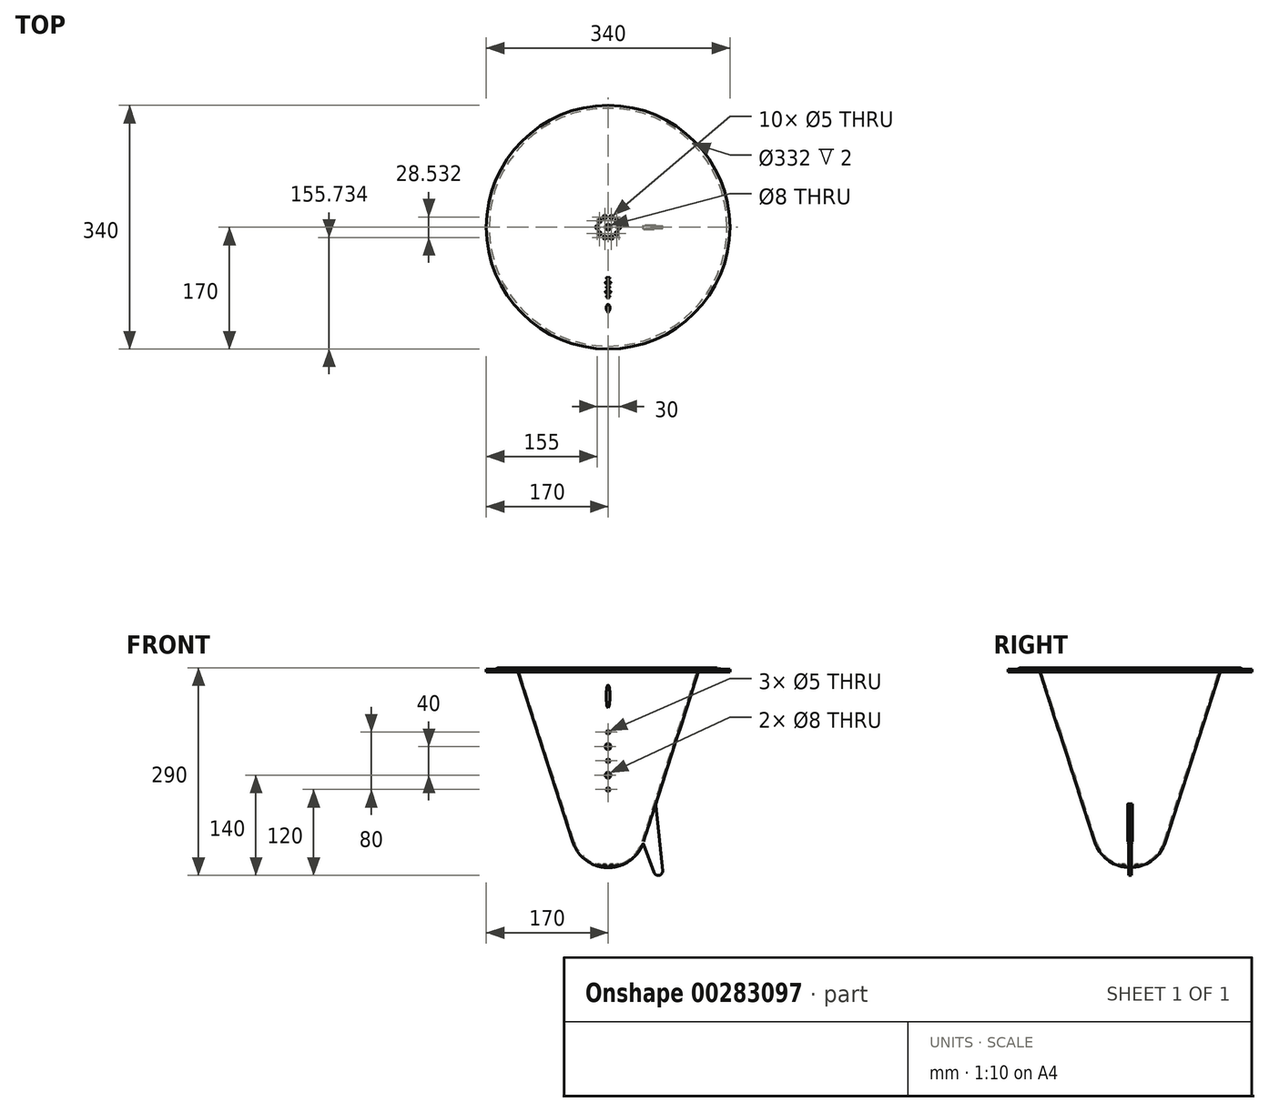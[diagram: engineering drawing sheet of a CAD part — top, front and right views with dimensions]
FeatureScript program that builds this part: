
annotation { "Feature Type Name" : "Feature", "Feature Type Description" : "" }
export const myFeature = defineFeature(function(context is Context, id is Id, definition is map)
    precondition{}
    {
        {
            var Q0;
            Q0=qCreatedBy(makeId("Front.planeOp"),FACE);
            var sketch = newSketch(context, id + "F0", { "sketchPlane" : qUnion([Q0])});
            skArc(sketch, "E0", {"start": v(0, -275) * mm, "mid": v(29.44, -265.41) * mm, "end": v(47.6, -240.33) * mm});
            skLineSegment(sketch, "E1", {"start": v(128.28, 0) * mm, "end": v(133.37, 0) * mm});
            skLineSegment(sketch, "E2.0", {"start": v(24.32, 2) * mm, "end": v(176.57, 2) * mm, "construction": true});
            skArc(sketch, "E3", {"start": v(155.32, 1) * mm, "mid": v(151.83, 2) * mm, "end": v(148.4, 0.8) * mm});
            skArc(sketch, "E4", {"start": v(143.6, 0.8) * mm, "mid": v(140.17, 2) * mm, "end": v(136.68, 1) * mm});
            skArc(sketch, "E5.trimOffspring", {"start": v(143.6, 0.8) * mm, "mid": v(146, 0) * mm, "end": v(148.4, 0.8) * mm});
            skLineSegment(sketch, "E6.trimOffspring", {"start": v(158.63, 0) * mm, "end": v(170, 0) * mm});
            skLineSegment(sketch, "E7", {"start": v(170, 0) * mm, "end": v(170, -4) * mm});
            skLineSegment(sketch, "E8", {"start": v(170, -4) * mm, "end": v(166, -4) * mm});
            skLineSegment(sketch, "E9", {"start": v(166, -4) * mm, "end": v(166, -2) * mm});
            skPoint(sketch, "E10.visualSharp", {"position": v(135.53, 0) * mm});
            skArc(sketch, "E10.filletArc", {"start": v(133.37, 0) * mm, "mid": v(135.1, 0.26) * mm, "end": v(136.68, 1) * mm});
            skPoint(sketch, "E11.visualSharp", {"position": v(156.47, 0) * mm});
            skArc(sketch, "E11.filletArc", {"start": v(155.32, 1) * mm, "mid": v(156.9, 0.26) * mm, "end": v(158.63, 0) * mm});
            skArc(sketch, "E12.0", {"start": v(154.21, -0.67) * mm, "mid": v(156.32, -1.66) * mm, "end": v(158.63, -2) * mm});
            skArc(sketch, "E12.1", {"start": v(154.21, -0.67) * mm, "mid": v(151.88, 0) * mm, "end": v(149.6, -0.8) * mm});
            skLineSegment(sketch, "E12.2", {"start": v(128.28, -2) * mm, "end": v(133.37, -2) * mm});
            skArc(sketch, "E12.3", {"start": v(133.37, -2) * mm, "mid": v(135.68, -1.66) * mm, "end": v(137.79, -0.67) * mm});
            skArc(sketch, "E12.4", {"start": v(142.4, -0.8) * mm, "mid": v(140.12, 0) * mm, "end": v(137.79, -0.67) * mm});
            skArc(sketch, "E12.5", {"start": v(142.4, -0.8) * mm, "mid": v(146, -2) * mm, "end": v(149.6, -0.8) * mm});
            skLineSegment(sketch, "E13", {"start": v(166, -2) * mm, "end": v(158.63, -2) * mm});
            skLineSegment(sketch, "E14", {"start": v(124, -3.12) * mm, "end": v(47.6, -240.33) * mm});
            skLineSegment(sketch, "E15", {"start": v(0, -225) * mm, "end": v(0, -275) * mm, "construction": true});
            skLineSegment(sketch, "E16.0", {"start": v(125.9, -3.73) * mm, "end": v(49.5, -240.94) * mm});
            skArc(sketch, "E16.1", {"start": v(0, -277) * mm, "mid": v(30.62, -267.03) * mm, "end": v(49.5, -240.94) * mm});
            skLineSegment(sketch, "E17", {"start": v(0, -275) * mm, "end": v(0, -277) * mm});
            skArc(sketch, "E18.filletArc", {"start": v(128.28, -2) * mm, "mid": v(126.8, -2.48) * mm, "end": v(125.9, -3.73) * mm});
            skPoint(sketch, "E19.visualSharp", {"position": v(125, 0) * mm});
            skArc(sketch, "E19.filletArc", {"start": v(128.28, 0) * mm, "mid": v(125.63, -0.86) * mm, "end": v(124, -3.12) * mm});
            skSolve(sketch);
        }
        {
            var Q0;
            Q0 = qSketchRegion(id + "F0", true);
            var Q1;
            Q1=sQuery(id+"F0.wireOp",EDGE,"E15");
            revolve(context, id + "F1", {"entities" : qUnion([Q0]), "axis" : qUnion([Q1]), "revolveType" : RevolveType.FULL});
        }
        {
            var Q0;
            Q0=qCreatedBy(makeId("Top.planeOp"),FACE);
            var sketch = newSketch(context, id + "F2", { "sketchPlane" : qUnion([Q0])});
            skCircle(sketch, "E20", {"center": v(0, 0) * mm, "radius": 4 * mm});
            skCircle(sketch, "E21", {"center": v(15, 0) * mm, "radius": 2.5 * mm});
            skCircle(sketch, "E22.1.0", {"center": v(12.14, 8.82) * mm, "radius": 2.5 * mm});
            skCircle(sketch, "E22.2.0", {"center": v(4.64, 14.27) * mm, "radius": 2.5 * mm});
            skCircle(sketch, "E22.3.0", {"center": v(-4.64, 14.27) * mm, "radius": 2.5 * mm});
            skCircle(sketch, "E22.4.0", {"center": v(-12.14, 8.82) * mm, "radius": 2.5 * mm});
            skCircle(sketch, "E22.5.0", {"center": v(-15, 0) * mm, "radius": 2.5 * mm});
            skCircle(sketch, "E22.6.0", {"center": v(-12.14, -8.82) * mm, "radius": 2.5 * mm});
            skCircle(sketch, "E22.7.0", {"center": v(-4.64, -14.27) * mm, "radius": 2.5 * mm});
            skCircle(sketch, "E22.8.0", {"center": v(4.64, -14.27) * mm, "radius": 2.5 * mm});
            skCircle(sketch, "E22.9.0", {"center": v(12.14, -8.82) * mm, "radius": 2.5 * mm});
            skSolve(sketch);
        }
        {
            var Q0;
            Q0 = qSketchRegion(id + "F2", true);
            extrude(context, id + "F3", {"entities" : qUnion([Q0]), "operationType" : NewBodyOperationType.REMOVE, "endBound" : BoundingType.THROUGH_ALL, "oppositeDirection" : true, "depth" : 25 * mm});
        }
        {
            var Q0;
            Q0=qCreatedBy(makeId("Front.planeOp"),FACE);
            var sketch = newSketch(context, id + "F4", { "sketchPlane" : qUnion([Q0])});
            skLineSegment(sketch, "E23", {"start": v(0, 0) * mm, "end": v(0, -185.64) * mm, "construction": true});
            skEllipse(sketch, "E24", {"center": v(0, -38) * mm, "majorRadius": 16 * mm, "minorRadius": 2.5 * mm, "majorAxis": v(0, -1)});
            skCircle(sketch, "E25", {"center": v(0, -168) * mm, "radius": 2.5 * mm});
            skCircle(sketch, "E26", {"center": v(0, -88) * mm, "radius": 2.5 * mm});
            skCircle(sketch, "E27", {"center": v(0, -148) * mm, "radius": 4 * mm});
            skCircle(sketch, "E28", {"center": v(0, -128) * mm, "radius": 2.5 * mm});
            skCircle(sketch, "E29", {"center": v(0, -108) * mm, "radius": 4 * mm});
            skSolve(sketch);
        }
        {
            var Q0;
            Q0 = qSketchRegion(id + "F4", true);
            extrude(context, id + "F5", {"entities" : qUnion([Q0]), "operationType" : NewBodyOperationType.REMOVE, "endBound" : BoundingType.THROUGH_ALL, "depth" : 25 * mm});
        }
        {
            var Q0;
            Q0=qCreatedBy(makeId("Front.planeOp"),FACE);
            var sketch = newSketch(context, id + "F6", { "sketchPlane" : qUnion([Q0])});
            skLineSegment(sketch, "E30.0", {"start": v(66.55, -188) * mm, "end": v(49.5, -240.94) * mm});
            skArc(sketch, "E31.0", {"start": v(0, -277) * mm, "mid": v(30.62, -267.03) * mm, "end": v(49.5, -240.94) * mm});
            skLineSegment(sketch, "E32", {"start": v(66.55, -188) * mm, "end": v(75.97, -281.4) * mm});
            skArc(sketch, "E33", {"start": v(64.4, -284.13) * mm, "mid": v(71.38, -287.84) * mm, "end": v(75.97, -281.4) * mm});
            skLineSegment(sketch, "E34", {"start": v(70, -288) * mm, "end": v(129.27, -288) * mm, "construction": true});
            skLineSegment(sketch, "E35", {"start": v(48.79, -243) * mm, "end": v(64.4, -284.13) * mm});
            skLineSegment(sketch, "E36.0", {"start": v(24.32, 2) * mm, "end": v(176.57, 2) * mm, "construction": true});
            skLineSegment(sketch, "E37.0", {"start": v(66.55, -184.74) * mm, "end": v(48.54, -240.64) * mm});
            skLineSegment(sketch, "E38", {"start": v(48.79, -243) * mm, "end": v(48.54, -240.64) * mm});
            skLineSegment(sketch, "E39", {"start": v(66.55, -188) * mm, "end": v(66.55, -184.74) * mm});
            skPoint(sketch, "E40.orphan", {"position": v(125.9, -3.73) * mm});
            skSolve(sketch);
        }
        {
            var Q0;
            Q0 = qSketchRegion(id + "F6", true);
            extrude(context, id + "F7", {"entities" : qUnion([Q0]), "operationType" : NewBodyOperationType.ADD, "endBound" : BoundingType.SYMMETRIC, "depth" : 4 * mm});
        }
        {
            var Q0;
            Q0=makeQuery(id+"FGJo6OA5AEpU7Sm_1.2.F7.boolean.opBoolean","INTERSECT",EDGE,{"derivedFrom":[makeQuery(id+"F1.opRevolve","SWEPT_FACE",FACE,{"disambiguationData":[OSD([sQuery(id+"F0.wireOp",EDGE,"E16.0")])]}),makeQuery(id+"FGJo6OA5AEpU7Sm_1.2.F7.opExtrude","CAP_FACE",FACE,{"disambiguationData":[OSD([sQuery(id+"F6.wireOp",EDGE,"E32"),sQuery(id+"F6.wireOp",EDGE,"E33"),sQuery(id+"F6.wireOp",EDGE,"E35"),sQuery(id+"F6.wireOp",EDGE,"E37.0"),sQuery(id+"F6.wireOp",EDGE,"E38"),sQuery(id+"F6.wireOp",EDGE,"E39")])],"isStart":true})]});
            var Q1;
            Q1=makeQuery(id+"FGJo6OA5AEpU7Sm_1.1.F7.boolean.opBoolean","INTERSECT",EDGE,{"derivedFrom":[makeQuery(id+"F1.opRevolve","SWEPT_FACE",FACE,{"disambiguationData":[OSD([sQuery(id+"F0.wireOp",EDGE,"E16.0")])]}),makeQuery(id+"FGJo6OA5AEpU7Sm_1.1.F7.opExtrude","CAP_FACE",FACE,{"disambiguationData":[OSD([sQuery(id+"F6.wireOp",EDGE,"E32"),sQuery(id+"F6.wireOp",EDGE,"E33"),sQuery(id+"F6.wireOp",EDGE,"E35"),sQuery(id+"F6.wireOp",EDGE,"E37.0"),sQuery(id+"F6.wireOp",EDGE,"E38"),sQuery(id+"F6.wireOp",EDGE,"E39")])],"isStart":false})]});
            var Q2;
            Q2=makeQuery(id+"FGJo6OA5AEpU7Sm_1.2.F7.boolean.opBoolean","INTERSECT",EDGE,{"derivedFrom":[makeQuery(id+"F1.opRevolve","SWEPT_FACE",FACE,{"disambiguationData":[OSD([sQuery(id+"F0.wireOp",EDGE,"E16.0")])]}),makeQuery(id+"FGJo6OA5AEpU7Sm_1.2.F7.opExtrude","CAP_FACE",FACE,{"disambiguationData":[OSD([sQuery(id+"F6.wireOp",EDGE,"E32"),sQuery(id+"F6.wireOp",EDGE,"E33"),sQuery(id+"F6.wireOp",EDGE,"E35"),sQuery(id+"F6.wireOp",EDGE,"E37.0"),sQuery(id+"F6.wireOp",EDGE,"E38"),sQuery(id+"F6.wireOp",EDGE,"E39")])],"isStart":false})]});
            var Q3;
            Q3=makeQuery(id+"F7.boolean.opBoolean","INTERSECT",EDGE,{"derivedFrom":[makeQuery(id+"F1.opRevolve","SWEPT_FACE",FACE,{"disambiguationData":[OSD([sQuery(id+"F0.wireOp",EDGE,"E16.0")])]}),makeQuery(id+"F7.opExtrude","CAP_FACE",FACE,{"disambiguationData":[OSD([sQuery(id+"F6.wireOp",EDGE,"E32"),sQuery(id+"F6.wireOp",EDGE,"E33"),sQuery(id+"F6.wireOp",EDGE,"E35"),sQuery(id+"F6.wireOp",EDGE,"E37.0"),sQuery(id+"F6.wireOp",EDGE,"E38"),sQuery(id+"F6.wireOp",EDGE,"E39")])],"isStart":true})]});
            var Q4;
            Q4=makeQuery(id+"F7.boolean.opBoolean","INTERSECT",EDGE,{"derivedFrom":[makeQuery(id+"F1.opRevolve","SWEPT_FACE",FACE,{"disambiguationData":[OSD([sQuery(id+"F0.wireOp",EDGE,"E16.0")])]}),makeQuery(id+"F7.opExtrude","CAP_FACE",FACE,{"disambiguationData":[OSD([sQuery(id+"F6.wireOp",EDGE,"E32"),sQuery(id+"F6.wireOp",EDGE,"E33"),sQuery(id+"F6.wireOp",EDGE,"E35"),sQuery(id+"F6.wireOp",EDGE,"E37.0"),sQuery(id+"F6.wireOp",EDGE,"E38"),sQuery(id+"F6.wireOp",EDGE,"E39")])],"isStart":false})]});
            var Q5;
            Q5=makeQuery(id+"FGJo6OA5AEpU7Sm_1.1.F7.boolean.opBoolean","INTERSECT",EDGE,{"derivedFrom":[makeQuery(id+"F1.opRevolve","SWEPT_FACE",FACE,{"disambiguationData":[OSD([sQuery(id+"F0.wireOp",EDGE,"E16.0")])]}),makeQuery(id+"FGJo6OA5AEpU7Sm_1.1.F7.opExtrude","CAP_FACE",FACE,{"disambiguationData":[OSD([sQuery(id+"F6.wireOp",EDGE,"E32"),sQuery(id+"F6.wireOp",EDGE,"E33"),sQuery(id+"F6.wireOp",EDGE,"E35"),sQuery(id+"F6.wireOp",EDGE,"E37.0"),sQuery(id+"F6.wireOp",EDGE,"E38"),sQuery(id+"F6.wireOp",EDGE,"E39")])],"isStart":true})]});
            fillet(context, id + "F8", {"entities" : qUnion([Q0, Q1, Q2, Q3, Q4, Q5]), "radius" : 1 * mm, "tangentPropagation" : true, "allowEdgeOverflow" : false});
        }
    });
